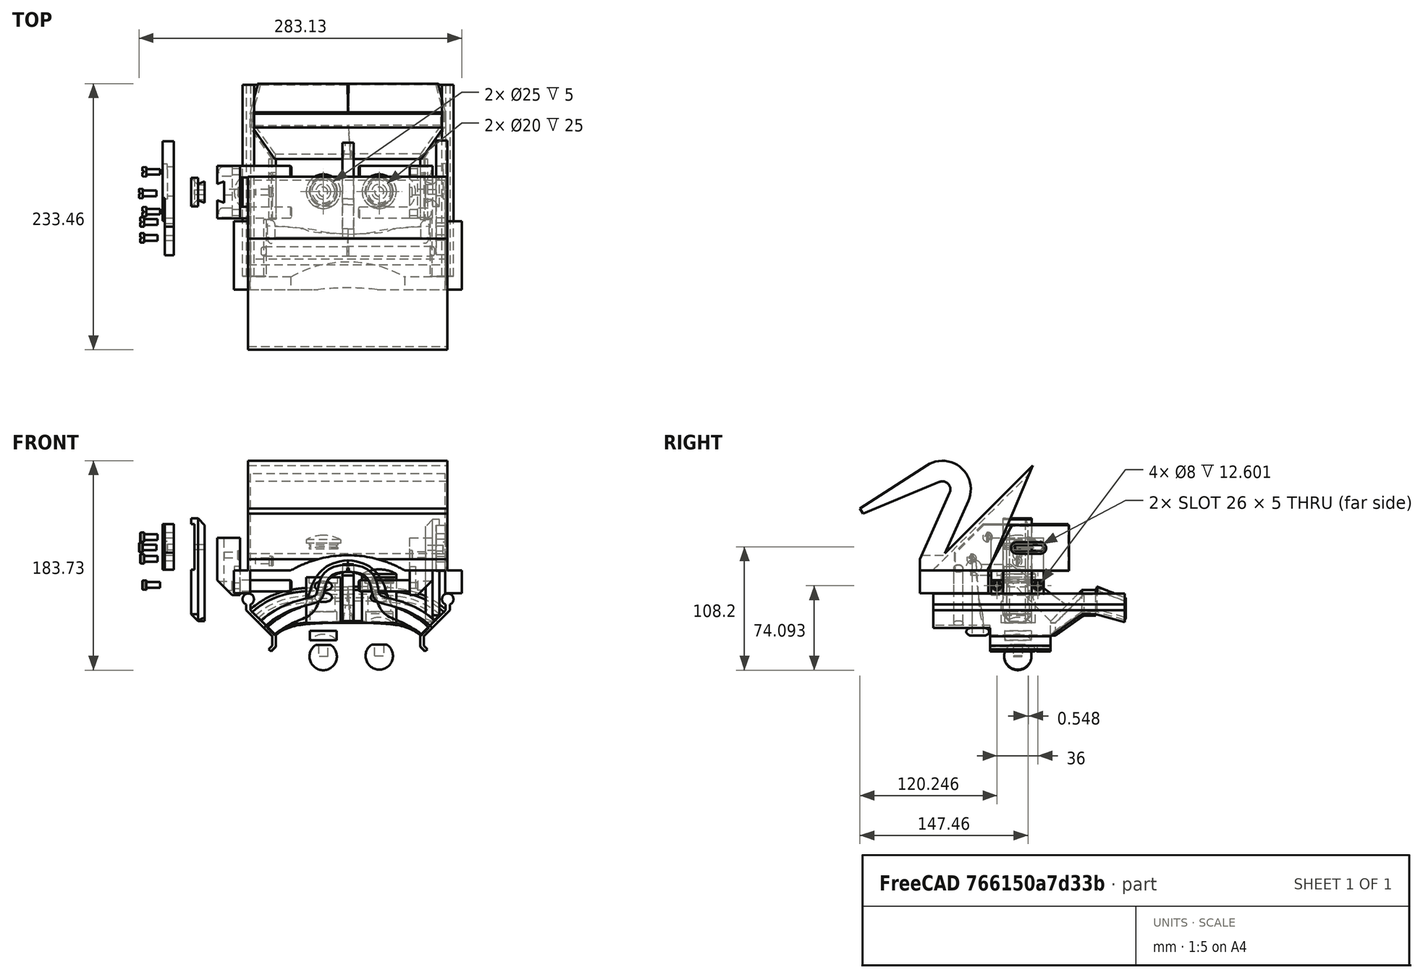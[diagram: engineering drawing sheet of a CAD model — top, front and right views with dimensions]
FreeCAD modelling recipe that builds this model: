
FCSTD DOCUMENT  (FreeCAD 0.18R16146 (Git))
Label: Exploded-View-01
License: All rights reserved
LicenseURL: http://en.wikipedia.org/wiki/All_rights_reserved
objects: App::FeaturePython×32, Part::FeaturePython×22, App::DocumentObjectGroup×1, TechDraw::DrawSVGTemplate×1, TechDraw::DrawPage×1
note: 22 computed .brp shape members not serialized (recipe doc carries the construction recipe); baked Part::Feature solids carry a one-line shape summary decoded from their .brp

FEATURE [Part::FeaturePython] b_TelescopeTube_001_  label="TelescopeTube_001"  # a2plus imported part (geometry in sourceFile) (typed FeaturePython)
  Placement = pos=(47.3988,19.7841,-44.3241) rot=(0,0,1;1.5708rad)
  a2p_Version = V0.1
  fixedPosition = true
  sourceFile = ./TelescopeTube.FCStd
  subassemblyImport = false
  timeLastImport = 1.56458e+09
  updateColors = true
FEATURE [Part::FeaturePython] b_ObjectiveLense_001_  label="ObjectiveLense_001"  # a2plus imported part (geometry in sourceFile) (typed FeaturePython)
  Placement = pos=(47.3988,19.7841,0.675946) rot=(0,0,1;0rad)
  a2p_Version = V0.1
  fixedPosition = false
  sourceFile = ./ObjectiveLense.FCStd
  subassemblyImport = false
  timeLastImport = 1.56457e+09
  updateColors = true
FEATURE [App::FeaturePython] circularEdge_001  label="circularEdge_001__TelescopeTube_001"  # a2plus constraint (typed FeaturePython)
  Object1 = b_ObjectiveLense_001_
  Object2 = b_TelescopeTube_001_
  ParentTreeObject = -> b_ObjectiveLense_001_
  SubElement1 = Edge4
  SubElement2 = Edge7
  Type = circularEdge
  directionConstraint = 1
  lockRotation = false
  offset = 0
FEATURE [App::FeaturePython] circularEdge_001_mirror  label="circularEdge_001__ObjectiveLense_001"  # a2plus constraint (typed FeaturePython)
  Object1 = b_ObjectiveLense_001_
  Object2 = b_TelescopeTube_001_
  ParentTreeObject = -> b_TelescopeTube_001_
  SubElement1 = Edge4
  SubElement2 = Edge7
  Type = circularEdge
  directionConstraint = 1
  lockRotation = false
  offset = 0
FEATURE [Part::FeaturePython] b_EyePiceLense_001_  label="EyePiceLense_001"  # a2plus imported part (geometry in sourceFile) (typed FeaturePython)
  Placement = pos=(47.3988,19.7841,-79.3241) rot=(0,0,1;0rad)
  a2p_Version = V0.1
  fixedPosition = false
  sourceFile = ./EyePiceLense.FCStd
  subassemblyImport = false
  timeLastImport = 1.56457e+09
  updateColors = true
FEATURE [App::FeaturePython] circularEdge_002  label="circularEdge_002__TelescopeTube_001"  # a2plus constraint (typed FeaturePython)
  Object1 = b_EyePiceLense_001_
  Object2 = b_TelescopeTube_001_
  ParentTreeObject = -> b_EyePiceLense_001_
  SubElement1 = Edge1
  SubElement2 = Edge14
  Type = circularEdge
  directionConstraint = 1
  lockRotation = false
  offset = 0
FEATURE [App::FeaturePython] circularEdge_002_mirror  label="circularEdge_002__EyePiceLense_001"  # a2plus constraint (typed FeaturePython)
  Object1 = b_EyePiceLense_001_
  Object2 = b_TelescopeTube_001_
  ParentTreeObject = -> b_TelescopeTube_001_
  SubElement1 = Edge1
  SubElement2 = Edge14
  Type = circularEdge
  directionConstraint = 1
  lockRotation = false
  offset = 0
FEATURE [Part::FeaturePython] b_SlideBlock_001_  label="SlideBlock_001"  # a2plus imported part (geometry in sourceFile) (typed FeaturePython)
  Placement = pos=(-35.6734,19.1861,-14.6272) rot=(0,0,1;0rad)
  a2p_Version = V0.1
  fixedPosition = false
  sourceFile = ./SlideBlock.FCStd
  subassemblyImport = false
  timeLastImport = 1.56467e+09
  updateColors = true
FEATURE [Part::FeaturePython] b_SideSlide_001_  label="SideSlide_001"  # a2plus imported part (geometry in sourceFile) (typed FeaturePython)
  Placement = pos=(-65.6734,19.1861,-17.5204) rot=(0,0,1;3.14159rad)
  a2p_Version = V0.1
  fixedPosition = false
  sourceFile = ./SideSlide.FCStd
  subassemblyImport = false
  timeLastImport = 1.56466e+09
  updateColors = true
FEATURE [App::DocumentObjectGroup] Group
  Group = -> [b_TelescopeTube_001_,b_ObjectiveLense_001_,b_EyePiceLense_001_]
FEATURE [Part::FeaturePython] b_SlideBlock_001_001  label="SlideBlock_002"  # a2plus imported part (geometry in sourceFile) (typed FeaturePython)
  Placement = pos=(133.327,19.1861,-14.6272) rot=(0,0,1;3.14159rad)
  a2p_Version = V0.1
  fixedPosition = true
  sourceFile = ./SlideBlock.FCStd
  subassemblyImport = false
  timeLastImport = 1.56467e+09
  updateColors = true
FEATURE [Part::FeaturePython] b_SideSlide_001_001  label="SideSlide_002"  # a2plus imported part (geometry in sourceFile) (typed FeaturePython)
  Placement = pos=(146.327,19.1861,-18.5315) rot=(0,0,1;0rad)
  a2p_Version = V0.1
  fixedPosition = false
  sourceFile = ./SideSlide.FCStd
  subassemblyImport = false
  timeLastImport = 1.56466e+09
  updateColors = true
FEATURE [App::FeaturePython] planeCoincident_003  label="planeCoincident_003__SideSlide_002"  # a2plus constraint (typed FeaturePython)
  Object1 = b_SlideBlock_001_001
  Object2 = b_SideSlide_001_001
  ParentTreeObject = -> b_SlideBlock_001_001
  SubElement1 = Face16
  SubElement2 = Face11
  Type = plane
  directionConstraint = 1
  offset = 0
FEATURE [App::FeaturePython] planeCoincident_003_mirror  label="planeCoincident_003__SlideBlock_002"  # a2plus constraint (typed FeaturePython)
  Object1 = b_SlideBlock_001_001
  Object2 = b_SideSlide_001_001
  ParentTreeObject = -> b_SideSlide_001_001
  SubElement1 = Face16
  SubElement2 = Face11
  Type = plane
  directionConstraint = 1
  offset = 0
FEATURE [App::FeaturePython] planeCoincident_004  label="planeCoincident_004__SlideBlock_002"  # a2plus constraint (typed FeaturePython)
  Object1 = b_SideSlide_001_001
  Object2 = b_SlideBlock_001_001
  ParentTreeObject = -> b_SideSlide_001_001
  SubElement1 = Face19
  SubElement2 = Face17
  Type = plane
  directionConstraint = 1
  offset = 0
FEATURE [App::FeaturePython] planeCoincident_004_mirror  label="planeCoincident_004__SideSlide_002"  # a2plus constraint (typed FeaturePython)
  Object1 = b_SideSlide_001_001
  Object2 = b_SlideBlock_001_001
  ParentTreeObject = -> b_SlideBlock_001_001
  SubElement1 = Face19
  SubElement2 = Face17
  Type = plane
  directionConstraint = 1
  offset = 0
FEATURE [Part::FeaturePython] b_LeftMirrorMount_001_  label="LeftMirrorMount_001"  # a2plus imported part (geometry in sourceFile) (typed FeaturePython)
  Placement = pos=(151.327,14.4487,1.46848) rot=(0,0,1;0rad)
  a2p_Version = V0.1
  fixedPosition = false
  sourceFile = ./LeftMirrorMount.FCStd
  subassemblyImport = false
  timeLastImport = 1.56473e+09
  updateColors = true
FEATURE [App::FeaturePython] planeCoincident_005  label="planeCoincident_005__SideSlide_002"  # a2plus constraint (typed FeaturePython)
  Object1 = b_LeftMirrorMount_001_
  Object2 = b_SideSlide_001_001
  ParentTreeObject = -> b_LeftMirrorMount_001_
  SubElement1 = Face5
  SubElement2 = Face6
  Type = plane
  directionConstraint = 0
  offset = 0
FEATURE [App::FeaturePython] planeCoincident_005_mirror  label="planeCoincident_005__LeftMirrorMount_001"  # a2plus constraint (typed FeaturePython)
  Object1 = b_LeftMirrorMount_001_
  Object2 = b_SideSlide_001_001
  ParentTreeObject = -> b_SideSlide_001_001
  SubElement1 = Face5
  SubElement2 = Face6
  Type = plane
  directionConstraint = 0
  offset = 0
FEATURE [App::FeaturePython] planeCoincident_006  label="planeCoincident_006__SideSlide_002"  # a2plus constraint (typed FeaturePython)
  Object1 = b_LeftMirrorMount_001_
  Object2 = b_SideSlide_001_001
  ParentTreeObject = -> b_LeftMirrorMount_001_
  SubElement1 = Face2
  SubElement2 = Face7
  Type = plane
  directionConstraint = 0
  offset = 0
FEATURE [App::FeaturePython] planeCoincident_006_mirror  label="planeCoincident_006__LeftMirrorMount_001"  # a2plus constraint (typed FeaturePython)
  Object1 = b_LeftMirrorMount_001_
  Object2 = b_SideSlide_001_001
  ParentTreeObject = -> b_SideSlide_001_001
  SubElement1 = Face2
  SubElement2 = Face7
  Type = plane
  directionConstraint = 0
  offset = 0
FEATURE [Part::FeaturePython] b_RightMirrorMount_001_  label="RightMirrorMount_001"  # a2plus imported part (geometry in sourceFile) (typed FeaturePython)
  Placement = pos=(-88.6734,13.9002,2.47964) rot=(0,0,1;0rad)
  a2p_Version = V0.1
  fixedPosition = false
  sourceFile = ./RightMirrorMount.FCStd
  subassemblyImport = false
  timeLastImport = 1.56465e+09
  updateColors = true
FEATURE [Part::FeaturePython] b_TelescopeTube_001_001  label="TelescopeTube_002"  # a2plus imported part (geometry in sourceFile) (typed FeaturePython)
  Placement = pos=(96.3988,19.7841,-44.3241) rot=(0,0,1;1.5708rad)
  a2p_Version = V0.1
  fixedPosition = true
  sourceFile = ./TelescopeTube.FCStd
  subassemblyImport = false
  timeLastImport = 1.56458e+09
  updateColors = true
FEATURE [Part::FeaturePython] b_ObjectiveLense_001_001  label="ObjectiveLense_002"  # a2plus imported part (geometry in sourceFile) (typed FeaturePython)
  Placement = pos=(96.3988,19.7841,-29.3241) rot=(0,0,1;0rad)
  a2p_Version = V0.1
  fixedPosition = false
  sourceFile = ./ObjectiveLense.FCStd
  subassemblyImport = false
  timeLastImport = 1.56457e+09
  updateColors = true
FEATURE [App::FeaturePython] circularEdge_004  label="circularEdge_004__TelescopeTube_002"  # a2plus constraint (typed FeaturePython)
  Object1 = b_ObjectiveLense_001_001
  Object2 = b_TelescopeTube_001_001
  ParentTreeObject = -> b_ObjectiveLense_001_001
  SubElement1 = Edge4
  SubElement2 = Edge7
  Type = circularEdge
  directionConstraint = 1
  lockRotation = false
  offset = 0
FEATURE [App::FeaturePython] circularEdge_004_mirror  label="circularEdge_004__ObjectiveLense_002"  # a2plus constraint (typed FeaturePython)
  Object1 = b_ObjectiveLense_001_001
  Object2 = b_TelescopeTube_001_001
  ParentTreeObject = -> b_TelescopeTube_001_001
  SubElement1 = Edge4
  SubElement2 = Edge7
  Type = circularEdge
  directionConstraint = 1
  lockRotation = false
  offset = 0
FEATURE [Part::FeaturePython] b_EyePiceLense_001_001  label="EyePiceLense_002"  # a2plus imported part (geometry in sourceFile) (typed FeaturePython)
  Placement = pos=(96.3988,19.7841,-64.3241) rot=(0,0,1;0rad)
  a2p_Version = V0.1
  fixedPosition = false
  sourceFile = ./EyePiceLense.FCStd
  subassemblyImport = false
  timeLastImport = 1.56457e+09
  updateColors = true
FEATURE [App::FeaturePython] circularEdge_005  label="circularEdge_005__TelescopeTube_002"  # a2plus constraint (typed FeaturePython)
  Object1 = b_EyePiceLense_001_001
  Object2 = b_TelescopeTube_001_001
  ParentTreeObject = -> b_EyePiceLense_001_001
  SubElement1 = Edge1
  SubElement2 = Edge14
  Type = circularEdge
  directionConstraint = 1
  lockRotation = false
  offset = 0
FEATURE [App::FeaturePython] circularEdge_005_mirror  label="circularEdge_005__EyePiceLense_002"  # a2plus constraint (typed FeaturePython)
  Object1 = b_EyePiceLense_001_001
  Object2 = b_TelescopeTube_001_001
  ParentTreeObject = -> b_TelescopeTube_001_001
  SubElement1 = Edge1
  SubElement2 = Edge14
  Type = circularEdge
  directionConstraint = 1
  lockRotation = false
  offset = 0
FEATURE [Part::FeaturePython] b_HeadCoil3_001_  label="HeadCoil3_001"  # a2plus imported part (geometry in sourceFile) (typed FeaturePython)
  Placement = pos=(69.0543,29.2994,-89.4133) rot=(0,0,1;0rad)
  a2p_Version = V0.1
  fixedPosition = false
  sourceFile = ./HeadCoil3.FCStd
  subassemblyImport = false
  timeLastImport = 1.52664e+09
  updateColors = true
FEATURE [Part::FeaturePython] b_Eye_001_  label="Eye_001"  # a2plus imported part (geometry in sourceFile) (typed FeaturePython)
  Placement = pos=(96.4622,19.4922,-93.226) rot=(0,1,0;3.14159rad)
  a2p_Version = V0.1
  fixedPosition = false
  sourceFile = ./Eye.FCStd
  subassemblyImport = false
  timeLastImport = 1.52665e+09
  updateColors = true
FEATURE [Part::FeaturePython] b_Eye_001_001  label="Eye_002"  # a2plus imported part (geometry in sourceFile) (typed FeaturePython)
  Placement = pos=(47.2948,19.4922,-93.7192) rot=(1,0,0;3.14159rad)
  a2p_Version = V0.1
  fixedPosition = false
  sourceFile = ./Eye.FCStd
  subassemblyImport = false
  timeLastImport = 1.52665e+09
  updateColors = true
FEATURE [App::FeaturePython] planeCoincident_009  label="planeCoincident_009__SlideBlock_002"  # a2plus constraint (typed FeaturePython)
  Object1 = b_SideSlide_001_001
  Object2 = b_SlideBlock_001_001
  ParentTreeObject = -> b_SideSlide_001_001
  SubElement1 = Face11
  SubElement2 = Face16
  Type = plane
  directionConstraint = 1
  offset = 0
FEATURE [App::FeaturePython] planeCoincident_009_mirror  label="planeCoincident_009__SideSlide_002"  # a2plus constraint (typed FeaturePython)
  Object1 = b_SideSlide_001_001
  Object2 = b_SlideBlock_001_001
  ParentTreeObject = -> b_SlideBlock_001_001
  SubElement1 = Face11
  SubElement2 = Face16
  Type = plane
  directionConstraint = 1
  offset = 0
FEATURE [App::FeaturePython] planeCoincident_010  label="planeCoincident_010__SlideBlock_002"  # a2plus constraint (typed FeaturePython)
  Object1 = b_SideSlide_001_001
  Object2 = b_SlideBlock_001_001
  ParentTreeObject = -> b_SideSlide_001_001
  SubElement1 = Face19
  SubElement2 = Face17
  Type = plane
  directionConstraint = 1
  offset = 0
FEATURE [App::FeaturePython] planeCoincident_010_mirror  label="planeCoincident_010__SideSlide_002"  # a2plus constraint (typed FeaturePython)
  Object1 = b_SideSlide_001_001
  Object2 = b_SlideBlock_001_001
  ParentTreeObject = -> b_SlideBlock_001_001
  SubElement1 = Face19
  SubElement2 = Face17
  Type = plane
  directionConstraint = 1
  offset = 0
FEATURE [Part::FeaturePython] b_Mirror02_001_  label="Mirror02_001"  # a2plus imported part (geometry in sourceFile) (typed FeaturePython)
  Placement = pos=(68.8266,-44.4073,-38.2508) rot=(0,0,1;1.5708rad)
  a2p_Version = V0.1
  fixedPosition = true
  sourceFile = ./Mirror02.FCStd
  subassemblyImport = false
  timeLastImport = 1.56473e+09
  updateColors = true
FEATURE [App::FeaturePython] planeCoincident_011  label="planeCoincident_011__LeftMirrorMount_001"  # a2plus constraint (typed FeaturePython)
  Object1 = b_Mirror02_001_
  Object2 = b_LeftMirrorMount_001_
  ParentTreeObject = -> b_Mirror02_001_
  SubElement1 = Face9
  SubElement2 = Face4
  Type = plane
  directionConstraint = 1
  offset = 0
FEATURE [App::FeaturePython] planeCoincident_011_mirror  label="planeCoincident_011__Mirror02_001"  # a2plus constraint (typed FeaturePython)
  Object1 = b_Mirror02_001_
  Object2 = b_LeftMirrorMount_001_
  ParentTreeObject = -> b_LeftMirrorMount_001_
  SubElement1 = Face9
  SubElement2 = Face4
  Type = plane
  directionConstraint = 1
  offset = 0
FEATURE [App::FeaturePython] planeCoincident_001  label="planeCoincident_001__SlideBlock_001"  # a2plus constraint (typed FeaturePython)
  Object1 = b_SideSlide_001_
  Object2 = b_SlideBlock_001_
  ParentTreeObject = -> b_SideSlide_001_
  SubElement1 = Face11
  SubElement2 = Face16
  Type = plane
  directionConstraint = 1
  offset = 0
FEATURE [App::FeaturePython] planeCoincident_001_mirror  label="planeCoincident_001__SideSlide_001"  # a2plus constraint (typed FeaturePython)
  Object1 = b_SideSlide_001_
  Object2 = b_SlideBlock_001_
  ParentTreeObject = -> b_SlideBlock_001_
  SubElement1 = Face11
  SubElement2 = Face16
  Type = plane
  directionConstraint = 1
  offset = 0
FEATURE [App::FeaturePython] planeCoincident_002  label="planeCoincident_002__SlideBlock_001"  # a2plus constraint (typed FeaturePython)
  Object1 = b_SideSlide_001_
  Object2 = b_SlideBlock_001_
  ParentTreeObject = -> b_SideSlide_001_
  SubElement1 = Face10
  SubElement2 = Face15
  Type = plane
  directionConstraint = 1
  offset = 0
FEATURE [App::FeaturePython] planeCoincident_002_mirror  label="planeCoincident_002__SideSlide_001"  # a2plus constraint (typed FeaturePython)
  Object1 = b_SideSlide_001_
  Object2 = b_SlideBlock_001_
  ParentTreeObject = -> b_SlideBlock_001_
  SubElement1 = Face10
  SubElement2 = Face15
  Type = plane
  directionConstraint = 1
  offset = 0
FEATURE [App::FeaturePython] planeCoincident_007  label="planeCoincident_007__SideSlide_001"  # a2plus constraint (typed FeaturePython)
  Object1 = b_RightMirrorMount_001_
  Object2 = b_SideSlide_001_
  ParentTreeObject = -> b_RightMirrorMount_001_
  SubElement1 = Face4
  SubElement2 = Face7
  Type = plane
  directionConstraint = 1
  offset = 0
FEATURE [App::FeaturePython] planeCoincident_007_mirror  label="planeCoincident_007__RightMirrorMount_001"  # a2plus constraint (typed FeaturePython)
  Object1 = b_RightMirrorMount_001_
  Object2 = b_SideSlide_001_
  ParentTreeObject = -> b_SideSlide_001_
  SubElement1 = Face4
  SubElement2 = Face7
  Type = plane
  directionConstraint = 1
  offset = 0
FEATURE [App::FeaturePython] planeCoincident_008  label="planeCoincident_008__SideSlide_001"  # a2plus constraint (typed FeaturePython)
  Object1 = b_RightMirrorMount_001_
  Object2 = b_SideSlide_001_
  ParentTreeObject = -> b_RightMirrorMount_001_
  SubElement1 = Face5
  SubElement2 = Face6
  Type = plane
  directionConstraint = 0
  offset = 0
FEATURE [App::FeaturePython] planeCoincident_008_mirror  label="planeCoincident_008__RightMirrorMount_001"  # a2plus constraint (typed FeaturePython)
  Object1 = b_RightMirrorMount_001_
  Object2 = b_SideSlide_001_
  ParentTreeObject = -> b_SideSlide_001_
  SubElement1 = Face5
  SubElement2 = Face6
  Type = plane
  directionConstraint = 0
  offset = 0
FEATURE [App::FeaturePython] planeCoincident_012  label="planeCoincident_012__Mirror02_001"  # a2plus constraint (typed FeaturePython)
  Object1 = b_RightMirrorMount_001_
  Object2 = b_Mirror02_001_
  ParentTreeObject = -> b_RightMirrorMount_001_
  SubElement1 = Face2
  SubElement2 = Face7
  Type = plane
  directionConstraint = 0
  offset = 0
FEATURE [App::FeaturePython] planeCoincident_012_mirror  label="planeCoincident_012__RightMirrorMount_001"  # a2plus constraint (typed FeaturePython)
  Object1 = b_RightMirrorMount_001_
  Object2 = b_Mirror02_001_
  ParentTreeObject = -> b_Mirror02_001_
  SubElement1 = Face2
  SubElement2 = Face7
  Type = plane
  directionConstraint = 0
  offset = 0
FEATURE [TechDraw::DrawSVGTemplate] Template
  EditableTexts = Designed_by_Name=Designed by Name; Drawing_number=Drawing number; FC-Date=Date; FC-SC=Scale; FC-SH=Sheet; FC-Title=Title; Subtitle=Subtitle; Weight=Weight
  Height = 210
  Orientation = 1
  Width = 297
FEATURE [TechDraw::DrawPage] Page
  KeepUpdated = true
  ProjectionType = 0
  Template = -> Template
FEATURE [Part::FeaturePython] Screw  label="M5x12-Screw"  # Fasteners workbench fastener (typed FeaturePython)
  Placement = pos=(-111,18,2) rot=(0,-1,0;1.5708rad)
  diameter = 7
  invert = false
  length = 3
  matchOuter = false
  offset = 0
  thread = false
  type = 4
FEATURE [Part::FeaturePython] Screw001  label="M5x12-Screw001"  # Fasteners workbench fastener (typed FeaturePython)
  Placement = pos=(2.2e-15,19,-10) rot=(0,1,0;1.5708rad)
  diameter = 7
  invert = false
  length = 3
  matchOuter = false
  offset = 0
  thread = false
  type = 4
FEATURE [Part::FeaturePython] Screw002  label="M5x12-Screw009"  # Fasteners workbench fastener (typed FeaturePython)
  Placement = pos=(-110,-7,11) rot=(0,-1,0;1.5708rad)
  diameter = 7
  invert = false
  length = 3
  matchOuter = false
  offset = 0
  thread = false
  type = 4
FEATURE [Part::FeaturePython] Screw003  label="M5x12-Screw005"  # Fasteners workbench fastener (typed FeaturePython)
  Placement = pos=(-110,-21,-8) rot=(0,-1,0;1.5708rad)
  diameter = 7
  invert = false
  length = 3
  matchOuter = false
  offset = 0
  thread = false
  type = 4
FEATURE [Part::FeaturePython] Screw004  label="M5x12-Screw008"  # Fasteners workbench fastener (typed FeaturePython)
  Placement = pos=(-108,2,-31) rot=(0,-1,0;1.5708rad)
  diameter = 7
  invert = false
  length = 3
  matchOuter = false
  offset = 0
  thread = false
  type = 4
FEATURE [Part::FeaturePython] Screw005  label="M5x12-Screw010"  # Fasteners workbench fastener (typed FeaturePython)
  Placement = pos=(-108,37,-31) rot=(0,-1,0;1.5708rad)
  diameter = 7
  invert = false
  length = 3
  matchOuter = false
  offset = 0
  thread = false
  type = 4
